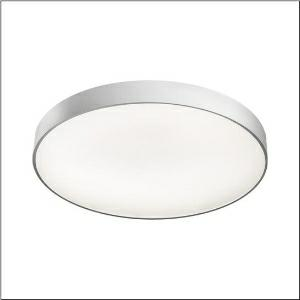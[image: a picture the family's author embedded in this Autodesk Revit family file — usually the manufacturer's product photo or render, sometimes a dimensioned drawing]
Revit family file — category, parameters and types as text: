
# Revit family: round_21_l_51mr38nd0321s
name_source: partatom
category: Lighting Fixtures
units: mm (PartAtom-declared; Revit-internal decimal feet)

## family parameters
Cut with Voids When Loaded = No
Host = Face
Light Source = No
Part Type = Normal
Room Calculation Point = No
Round Connector Dimension = Use Diameter
Shared = No

## types (1)
- Round 21 L (1 x LED, 11740 lm, 88.2 W, 3000K)
    Apparent Load = 88 VA
    CIE Flux Codes = 66 90 98 71 100
    Color Rendering = 80
    Color Temperature = 3000K
    Default Elevation = 1800 mm
    Description = Round 21 L, wall and ceiling luminaire, primary optical cover: micro prismatic cover, of PMMA, transparent, CAT 2 (L<= 3000cd/m²), light emission: direct/indirect distribution, primary light characteristic: symmetric, installation type: suspended mounting, surface-mounted, LED, rated luminous flux: 11.740lm, luminous efficacy: 133lm/W, light colour: 830, colour temperature: 3000K, control gear: DALI 2, with terminal, 5-pole, mains connection: 230V, AC, 50/60Hz, rated input power: 88.2W, housing, of aluminium, coated, silver, diameter: 850mm, height: 62mm, protection rating (complete): IP40, insulation class (complete): insulation class I (protective earthing), certification: CE, impact resistance: IK04, permissible operating ambient temperature: -10..+35°C, packaging unit: 1 piece
    Height = 87 mm
    Lamp = 1 x LED
    Lamp Light Flux = 11740 lm
    Lamp Power = 88.2 W
    Lamp count = 1
    Length = 850 mm
    Luminous efficacy = 133 lm/W
    Manufacturer = Siteco
    ModVariant = No
    Model = 51MR38ND0321S
    Mounting Place = Ceiling
    Mounting Type = Surface mounted
    Number of Poles = 1
    OnlyDefault = Yes
    Power Factor = 1
    Product Name = Round 21 L
    Product group = wall and ceiling luminaire
    ProductGroupID = 304
    Protection Class = Protection class I
    Protection Degree = IP 40
    RLX_Detail_Level = 1
    RLX_Emergency_Light_Flux = 0 lm
    RLX_Emergency_Type = 0
    RLX_Emergency_Type_DB = No
    RlxData = <blob elided: 25165 chars, md5=3038fc89>
    Socket = socket
    Standby Power = 0 W
    System Light Flux = 11740 lm
    System Power = 88 W
    Type Comments = Product without accessories
    Type Image = l_1258322.jpg
    URL = http://relux.com
    VarID = ---
    Voltage = 0 V
    Weight = 0.00 kg
    Width = 0 mm  [stored 0 ft]

note: [stored X ft] marks values corroborated as IEEE doubles in the binary element streams (Revit-internal decimal feet)

## geometry (parser evidence)
native form markers: Blend x4, Sweep x13
no freeform markers — native parametric forms only
